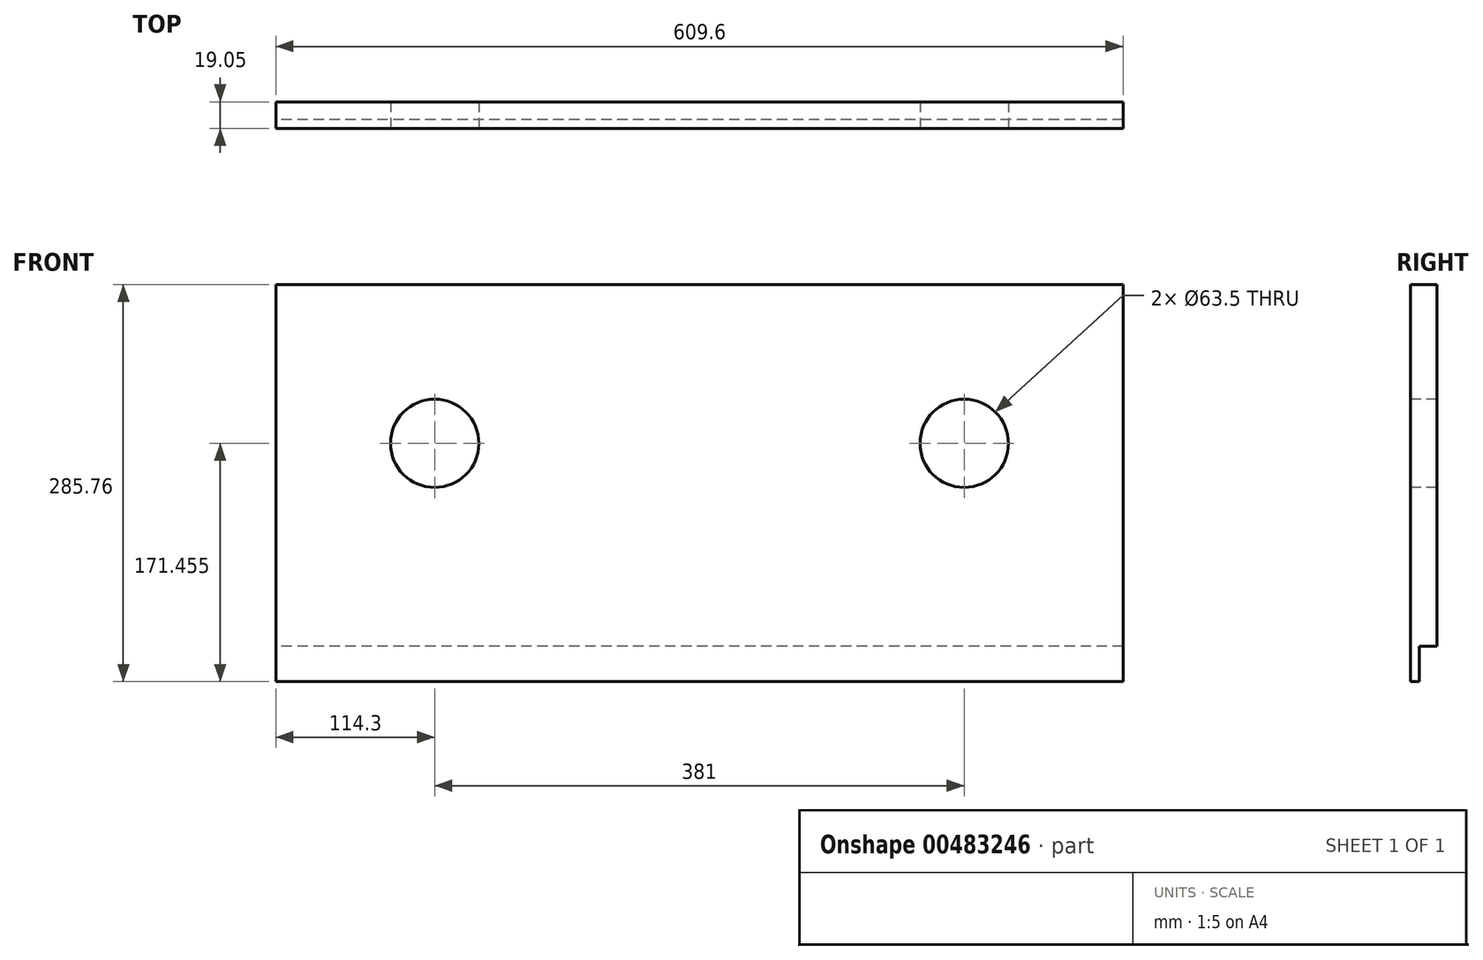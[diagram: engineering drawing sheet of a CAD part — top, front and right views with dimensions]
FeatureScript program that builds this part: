
annotation { "Feature Type Name" : "Feature", "Feature Type Description" : "" }
export const myFeature = defineFeature(function(context is Context, id is Id, definition is map)
    precondition{}
    {
        {
            var Q0;
            Q0=qCreatedBy(makeId("Front.planeOp"),FACE);
            var sketch = newSketch(context, id + "F0", { "sketchPlane" : qUnion([Q0])});
            skLineSegment(sketch, "E0.bottom", {"start": v(304.8, 142.88) * mm, "end": v(-304.8, 142.88) * mm});
            skLineSegment(sketch, "E0.top", {"start": v(304.8, -142.88) * mm, "end": v(-304.8, -142.88) * mm});
            skLineSegment(sketch, "E0.left", {"start": v(304.8, 142.87) * mm, "end": v(304.8, -142.88) * mm});
            skLineSegment(sketch, "E0.right", {"start": v(-304.8, 142.88) * mm, "end": v(-304.8, -142.88) * mm});
            skPoint(sketch, "E0.middle", {"position": v(0, 0) * mm});
            skSolve(sketch);
        }
        {
            var Q0;
            Q0 = qSketchRegion(id + "F0", true);
            extrude(context, id + "F1", {"entities" : qUnion([Q0]), "depth" : 19.05 * mm});
        }
        {
            var Q0;
            Q0=makeQuery(id+"F1.opExtrude","SWEPT_FACE",FACE,{"disambiguationData":[OSD([sQuery(id+"F0.wireOp",EDGE,"E0.right")])]});
            var sketch = newSketch(context, id + "F2", { "sketchPlane" : qUnion([Q0])});
            skLineSegment(sketch, "E1.bottom", {"start": v(0, -142.88) * mm, "end": v(12.7, -142.88) * mm});
            skLineSegment(sketch, "E1.top", {"start": v(0, -117.48) * mm, "end": v(12.7, -117.48) * mm});
            skLineSegment(sketch, "E1.left", {"start": v(0, -142.88) * mm, "end": v(0, -117.48) * mm});
            skLineSegment(sketch, "E1.right", {"start": v(12.7, -142.88) * mm, "end": v(12.7, -117.48) * mm});
            skSolve(sketch);
        }
        {
            var Q0;
            Q0 = qSketchRegion(id + "F2", true);
            extrude(context, id + "F3", {"entities" : qUnion([Q0]), "operationType" : NewBodyOperationType.REMOVE, "endBound" : BoundingType.THROUGH_ALL, "oppositeDirection" : true, "depth" : 25.4 * mm});
        }
        {
            var Q0;
            Q0=makeQuery(id+"F1.opExtrude","CAP_FACE",FACE,{"disambiguationData":[OSD([sQuery(id+"F0.wireOp",EDGE,"E0.bottom"),sQuery(id+"F0.wireOp",EDGE,"E0.top"),sQuery(id+"F0.wireOp",EDGE,"E0.left"),sQuery(id+"F0.wireOp",EDGE,"E0.right")])],"isStart":false});
            var sketch = newSketch(context, id + "F4", { "sketchPlane" : qUnion([Q0])});
            skCircle(sketch, "E2", {"center": v(-190.5, 28.57) * mm, "radius": 31.75 * mm});
            skCircle(sketch, "E3", {"center": v(190.5, 28.57) * mm, "radius": 31.75 * mm});
            skSolve(sketch);
        }
        {
            var Q0;
            Q0 = qSketchRegion(id + "F4", true);
            extrude(context, id + "F5", {"entities" : qUnion([Q0]), "operationType" : NewBodyOperationType.REMOVE, "endBound" : BoundingType.THROUGH_ALL, "oppositeDirection" : true, "depth" : 25.4 * mm});
        }
    });
